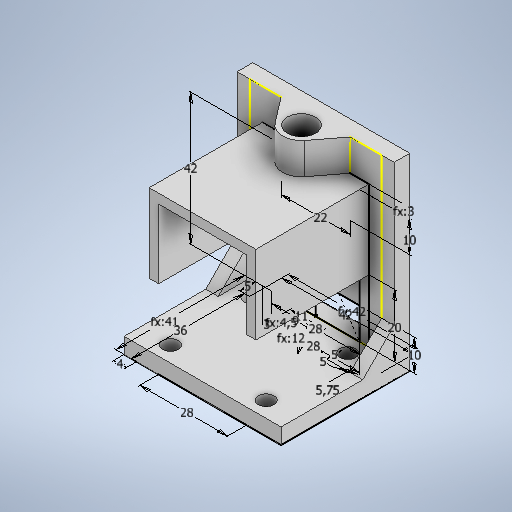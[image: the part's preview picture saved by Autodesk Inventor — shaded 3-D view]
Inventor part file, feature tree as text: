
AUTODESK INVENTOR PART (.ipt)
format: ipt  version: 2025 (Build 290162000, 162)  size: 377,856 bytes
history: native  units: mm
features: extrude x10, sketch x2, chamfer x2, other x1, projected_geometry x1
ambient origin geometry x8: Origin, YZ Plane, XZ Plane, XY Plane, X Axis, Y Axis, Z Axis, Center Point
bodies: Body1 (feature_tree)
feature tree (16):
  other  "Bryła1"
  sketch  "Szkic1"
  extrude  "Wyciągnięcie proste1"  Depth=5.0mm
  extrude  "Wyciągnięcie proste2"  Depth=5.75mm
  extrude  "Wyciągnięcie proste3"  Depth=5.0mm
  extrude  "Wyciągnięcie proste4"  Depth=5.0mm
  sketch  "Szkic3"
  extrude  "Wyciągnięcie proste5"  Depth=42.0mm
  extrude  "Wyciągnięcie proste6"  Depth=4.5mm
  extrude  "Wyciągnięcie proste7"  Depth=12.0mm
  extrude  "Wyciągnięcie proste8"  Depth=11.0mm
  extrude  "Wyciągnięcie proste9"  Depth=5.0mm TaperAngle=0.0deg
  extrude  "Wyciągnięcie proste10"  Depth=60.0mm TaperAngle=0.0deg
  chamfer  "Faza1"  Distance=50.0mm
  chamfer  "Faza2"  Distance=5.0mm
  projected_geometry  "Pętla rzutowana1"
